# Revit family: okamura_CRC7BK-CRD7BK_Shibusa_Hi-Back Polished Frame Fully Upholstered_1
name_source: partatom
category: Furniture
revit_build: Autodesk Revit 2017 (Build: 20160225_1515(x64)
units: mm (PartAtom-declared; Revit-internal decimal feet)

## family parameters
Always vertical = Yes
Cut with Voids When Loaded = No
OmniClass Number = 23.40.20.00
OmniClass Title = General Furniture and Specialties
Room Calculation Point = No
Shared = No
Work Plane-Based = No

## types (28) — shared parameters
Armrest Pad = okm_G721
Assembly Code = E2020200
Base and Frame = okm_silver FX4
Caster and other = okm_G155
D = 575 mm
Gas Lift = okm_G721
H = 1050 mm
Keynote = 12490
Kind = Chair
Manufacturer = Okamura Corporation
Product Categories = Office Seating
URL = http://www.okamura.co.jp
W = 650 mm

## per-type parameters (varying)
| type | Product Number | Seat and Backrest |
| FWJ7(Beige)_Hard caster | CRC7BK | okm_FWJ7 |
| FWK3(Light Grey)_Hard caster | CRC7BK | okm_FWK3 |
| FWK1(Dark Grey)_Hard caster | CRC7BK | okm_FWK1 |
| FWJ1(Black)_Hard caster | CRC7BK | okm_FWJ1 |
| FWK4(Dark Blue)_Hard caster | CRC7BK | okm_FWK4 |
| FWJ4（Aqua Blue）_Hard caster | CRC7BK | okm_FWJ4 |
| FWK6(Blue Green)_Hard caster | CRC7BK | okm_FWK6 |
| FWJ5(Green)_Hard caster | CRC7BK | okm_FWJ5 |
| FWJ6(Yellow)_Hard caster | CRC7BK | okm_FWJ6 |
| FWJ9(Orange Red)_Hard caster | CRC7BK | okm_FWJ9 |
| PC18(White)_Hard caster | CRC7BK | okm_PC18 |
| PD98(Camel)_Hard caster | CRC7BK | okm_PD98 |
| PD97(Dark Brown)_Hard caster | CRC7BK | okm_PD97 |
| P676 (Black)_Hard caster | CRC7BK | okm_P676 |
| PD97(Dark Brown)_Soft caster | CRD7BK | okm_PD97 |
| FWJ1(Black)_Soft caster | CRD7BK | okm_FWJ1 |
| FWJ4（Aqua Blue）_Soft caster | CRD7BK | okm_FWJ4 |
| FWJ5(Green)_Soft caster | CRD7BK | okm_FWJ5 |
| FWJ6(Yellow)_Soft caster | CRD7BK | okm_FWJ6 |
| FWJ7(Beige)_Soft caster | CRD7BK | okm_FWJ7 |
| FWJ9(Orange Red)_Soft caster | CRD7BK | okm_FWJ9 |
| FWK1(Dark Grey)_Soft caster | CRD7BK | okm_FWK1 |
| FWK3(Light Grey)_Soft caster | CRD7BK | okm_FWK3 |
| FWK4(Dark Blue)_Soft caster | CRD7BK | okm_FWK4 |
| FWK6(Blue Green)_Soft caster | CRD7BK | okm_FWK6 |
| P676 (Black)_Soft caster | CRD7BK | okm_P676 |
| PC18(White)_Soft caster | CRD7BK | okm_PC18 |
| PD98(Camel)_Soft caster | CRD7BK | okm_PD98 |
